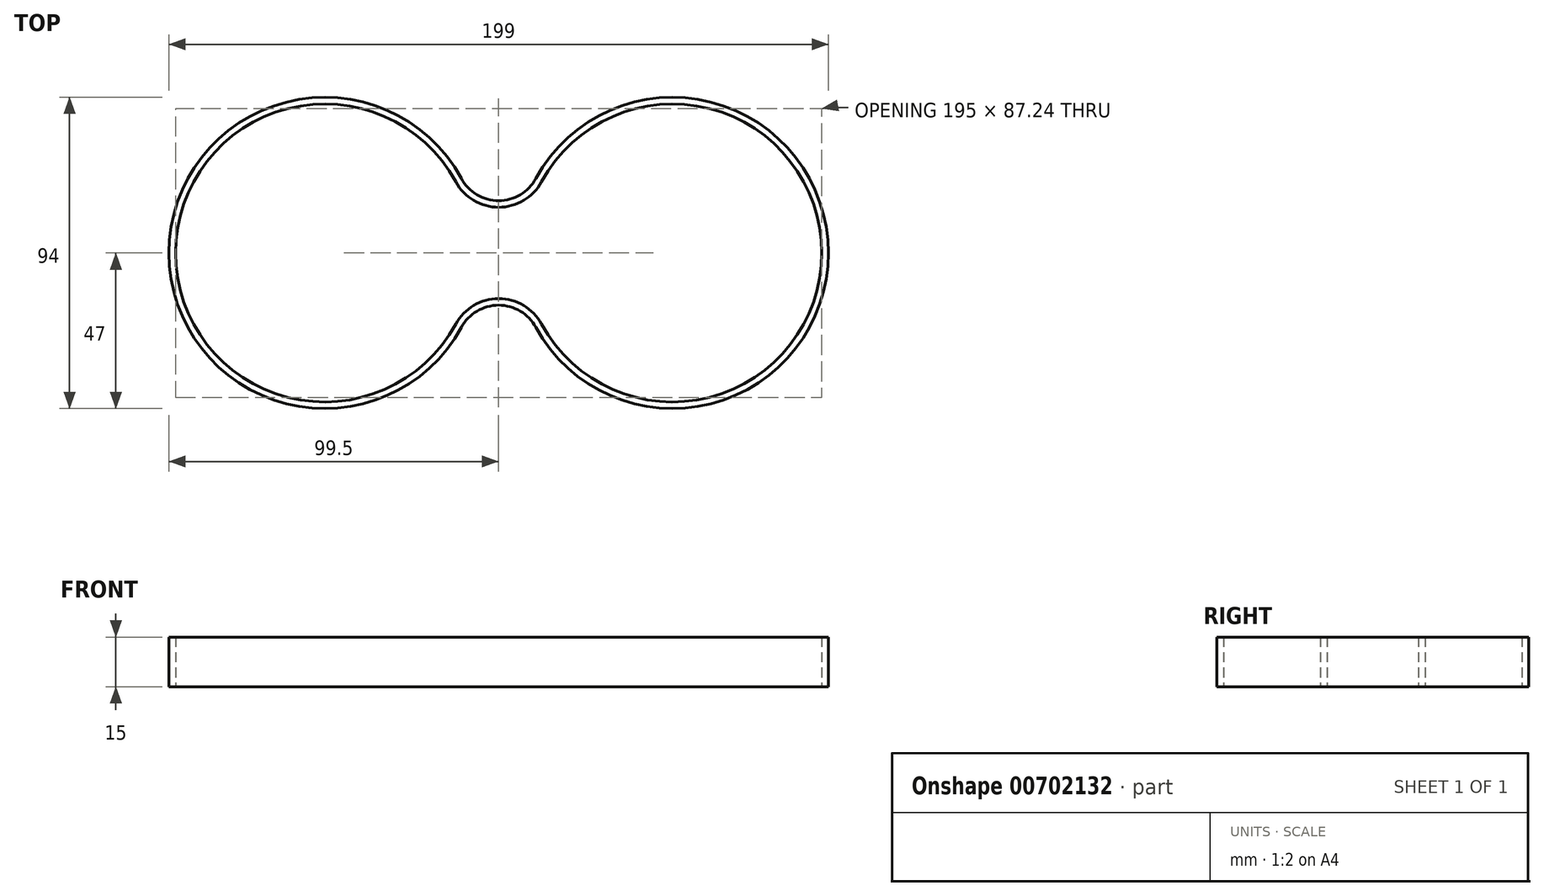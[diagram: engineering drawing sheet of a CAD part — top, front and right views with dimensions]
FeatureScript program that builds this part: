
annotation { "Feature Type Name" : "Feature", "Feature Type Description" : "" }
export const myFeature = defineFeature(function(context is Context, id is Id, definition is map)
    precondition{}
    {
        {
            var Q0;
            Q0=qCreatedBy(makeId("Top.planeOp"),FACE);
            var sketch = newSketch(context, id + "F0", { "sketchPlane" : qUnion([Q0])});
            skArc(sketch, "E0", {"start": v(39.57, 21.43) * mm, "mid": v(-45, 0) * mm, "end": v(39.57, -21.43) * mm});
            skArc(sketch, "E1", {"start": v(65.43, -21.43) * mm, "mid": v(150, 0) * mm, "end": v(65.43, 21.43) * mm});
            skArc(sketch, "E2", {"start": v(41.32, 22.4) * mm, "mid": v(-47, 0) * mm, "end": v(41.32, -22.4) * mm});
            skArc(sketch, "E3", {"start": v(60.98, -16.46) * mm, "mid": v(151.89, -3.26) * mm, "end": v(63.68, 22.4) * mm});
            skArc(sketch, "E4", {"start": v(63.73, -22.5) * mm, "mid": v(52.5, -15.78) * mm, "end": v(41.27, -22.5) * mm});
            skArc(sketch, "E5.MirrorCS", {"start": v(63.73, 22.5) * mm, "mid": v(52.5, 15.78) * mm, "end": v(41.27, 22.5) * mm});
            skArc(sketch, "E6.0", {"start": v(65.5, 21.55) * mm, "mid": v(52.5, 13.78) * mm, "end": v(39.5, 21.55) * mm});
            skArc(sketch, "E7.0", {"start": v(65.5, -21.55) * mm, "mid": v(52.5, -13.78) * mm, "end": v(39.5, -21.55) * mm});
            skSolve(sketch);
        }
        {
            var Q0;
            {var subQ4=sQuery(id+"F0.wireOp",EDGE,"E0");Q0=makeQuery(id+"F0.imprint","IMPRINT",FACE,{"disambiguationData":[TD([[makeQuery(id+"F0.imprint","IMPRINT",EDGE,{"derivedFrom":subQ4}),-1.0]])]});}
            extrude(context, id + "F1", {"entities" : qUnion([Q0]), "depth" : 15 * mm, "offsetDistance" : 25 * mm});
        }
    });
